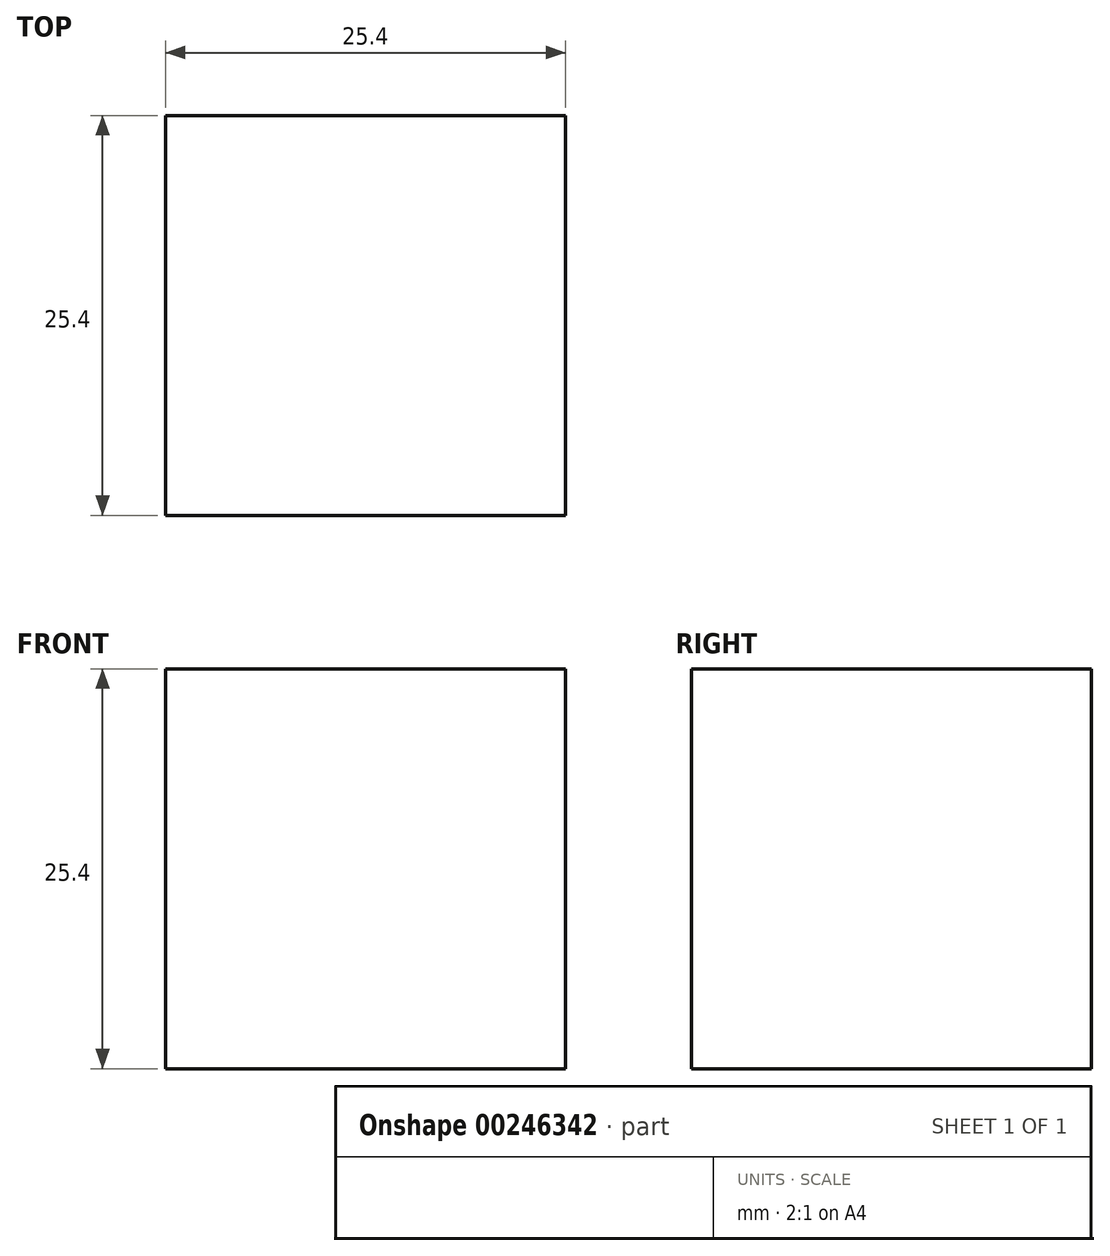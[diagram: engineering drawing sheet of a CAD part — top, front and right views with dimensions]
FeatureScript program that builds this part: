
annotation { "Feature Type Name" : "Feature", "Feature Type Description" : "" }
export const myFeature = defineFeature(function(context is Context, id is Id, definition is map)
    precondition{}
    {
        {
            var Q0;
            Q0=qCreatedBy(makeId("Front.planeOp"),FACE);
            var sketch = newSketch(context, id + "F0", { "sketchPlane" : qUnion([Q0])});
            skLineSegment(sketch, "E0", {"start": v(0, 0) * mm, "end": v(0, 25.4) * mm});
            skLineSegment(sketch, "E1", {"start": v(0, 25.4) * mm, "end": v(-25.4, 25.4) * mm});
            skLineSegment(sketch, "E2", {"start": v(-25.4, 25.4) * mm, "end": v(-25.4, 0) * mm});
            skLineSegment(sketch, "E3", {"start": v(-25.4, 0) * mm, "end": v(0, 0) * mm});
            skSolve(sketch);
        }
        {
            var Q0;
            Q0 = qSketchRegion(id + "F0", true);
            extrude(context, id + "F1", {"entities" : qUnion([Q0]), "depth" : 25.4 * mm});
        }
    });
